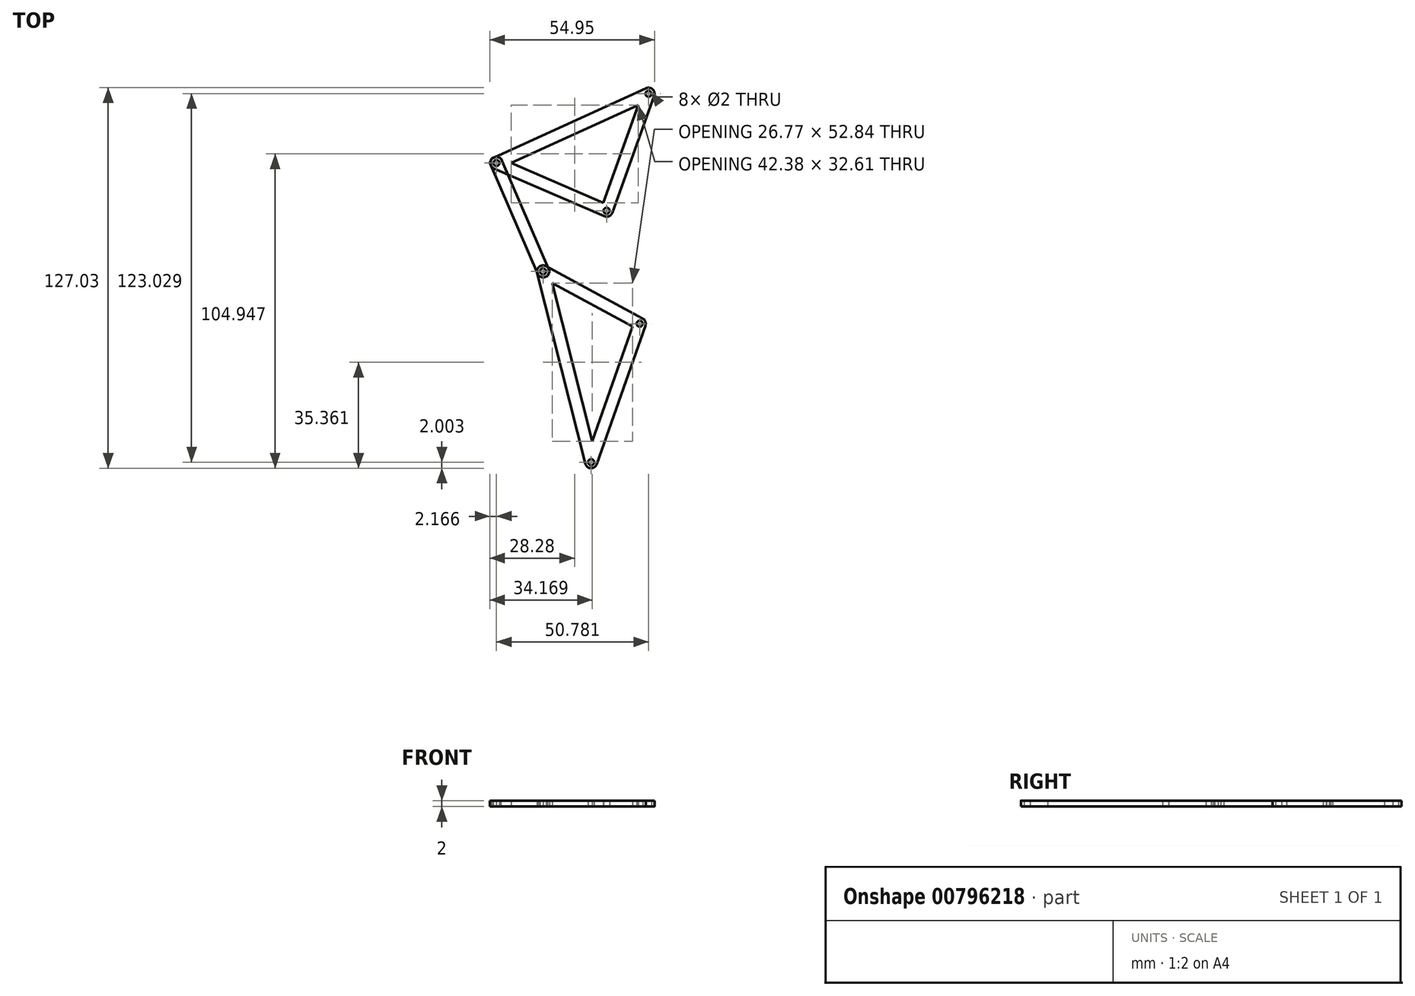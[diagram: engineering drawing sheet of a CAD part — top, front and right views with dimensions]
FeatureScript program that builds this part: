
annotation { "Feature Type Name" : "Feature", "Feature Type Description" : "" }
export const myFeature = defineFeature(function(context is Context, id is Id, definition is map)
    precondition{}
    {
        {
            var Q0;
            Q0=qCreatedBy(makeId("Top.planeOp"),FACE);
            var sketch = newSketch(context, id + "F0", { "sketchPlane" : qUnion([Q0])});
            skLineSegment(sketch, "E0", {"start": v(-38, -7.8) * mm, "end": v(-74.8, 8.14) * mm});
            skLineSegment(sketch, "E1", {"start": v(-74.8, 8.14) * mm, "end": v(-24.01, 31.27) * mm});
            skLineSegment(sketch, "E2", {"start": v(-24.01, 31.27) * mm, "end": v(-38, -7.8) * mm});
            skLineSegment(sketch, "E3", {"start": v(-24.01, 31.27) * mm, "end": v(15, 0) * mm});
            skLineSegment(sketch, "E4", {"start": v(15, 0) * mm, "end": v(0, 0) * mm});
            skLineSegment(sketch, "E5", {"start": v(-74.8, 8.14) * mm, "end": v(-59.23, -28.05) * mm});
            skLineSegment(sketch, "E6", {"start": v(-59.23, -28.05) * mm, "end": v(-26.95, -45.52) * mm});
            skLineSegment(sketch, "E7", {"start": v(-26.95, -45.52) * mm, "end": v(-38, -7.8) * mm});
            skLineSegment(sketch, "E8", {"start": v(-26.95, -45.52) * mm, "end": v(15, 0) * mm});
            skLineSegment(sketch, "E9", {"start": v(-59.23, -28.05) * mm, "end": v(-43.16, -91.76) * mm});
            skLineSegment(sketch, "E10", {"start": v(-43.16, -91.76) * mm, "end": v(-26.95, -45.52) * mm});
            skLineSegment(sketch, "E11", {"start": v(-38, -7.8) * mm, "end": v(0, -7.8) * mm, "construction": true});
            skLineSegment(sketch, "E12", {"start": v(0, -7.8) * mm, "end": v(0, 0) * mm, "construction": true});
            skSolve(sketch);
        }
        {
            assignVariable(context, id + "F1", {"name" : "thick", "anyValue" : 2});
        }
        {
            var Q0;
            Q0=qCreatedBy(makeId("Top.planeOp"),FACE);
            var sketch = newSketch(context, id + "F2", { "sketchPlane" : qUnion([Q0])});
            skCircle(sketch, "E13", {"center": v(-24.01, 31.27) * mm, "radius": 1 * mm});
            skCircle(sketch, "E14", {"center": v(-38, -7.8) * mm, "radius": 1 * mm});
            skCircle(sketch, "E15", {"center": v(-74.8, 8.14) * mm, "radius": 1 * mm});
            skArc(sketch, "E16", {"start": v(-75.62, 9.96) * mm, "mid": v(-76.8, 8.12) * mm, "end": v(-75.59, 6.3) * mm});
            skArc(sketch, "E17", {"start": v(-22.13, 30.6) * mm, "mid": v(-22.66, 32.74) * mm, "end": v(-24.84, 33.1) * mm});
            skArc(sketch, "E18", {"start": v(-38.8, -9.64) * mm, "mid": v(-37.2, -9.63) * mm, "end": v(-36.12, -8.47) * mm});
            skLineSegment(sketch, "E19", {"start": v(-75.62, 9.96) * mm, "end": v(-24.84, 33.1) * mm});
            skLineSegment(sketch, "E20", {"start": v(-22.13, 30.6) * mm, "end": v(-36.12, -8.47) * mm});
            skLineSegment(sketch, "E21", {"start": v(-38.8, -9.64) * mm, "end": v(-75.59, 6.3) * mm});
            skLineSegment(sketch, "E22.0", {"start": v(-69.87, 8.19) * mm, "end": v(-27.5, 27.5) * mm});
            skLineSegment(sketch, "E22.1", {"start": v(-39.16, -5.12) * mm, "end": v(-69.87, 8.19) * mm});
            skLineSegment(sketch, "E22.2", {"start": v(-27.5, 27.5) * mm, "end": v(-39.16, -5.12) * mm});
            skSolve(sketch);
        }
        {
            var Q0;
            Q0=makeQuery(id+"F2.imprint","IMPRINT",FACE,{"disambiguationData":[TD([[makeQuery(id+"F2.imprint","IMPRINT",EDGE,{"derivedFrom":sQuery(id+"F2.wireOp",EDGE,"E13")}),-1.0]])]});
            extrude(context, id + "F3", {"entities" : qUnion([Q0]), "depth" : (getVariable(context, 'thick')) * mm, "offsetDistance" : 25 * mm});
        }
        {
            var Q0;
            Q0=qCreatedBy(makeId("Top.planeOp"),FACE);
            var sketch = newSketch(context, id + "F4", { "sketchPlane" : qUnion([Q0])});
            skCircle(sketch, "E23", {"center": v(-26.95, -45.52) * mm, "radius": 1 * mm});
            skCircle(sketch, "E24", {"center": v(-43.16, -91.76) * mm, "radius": 1 * mm});
            skCircle(sketch, "E25", {"center": v(-59.23, -28.05) * mm, "radius": 1 * mm});
            skArc(sketch, "E26", {"start": v(-58.28, -26.3) * mm, "mid": v(-60.46, -26.47) * mm, "end": v(-61.17, -28.54) * mm});
            skArc(sketch, "E27", {"start": v(-25.06, -46.18) * mm, "mid": v(-25.09, -44.8) * mm, "end": v(-26, -43.76) * mm});
            skArc(sketch, "E28", {"start": v(-45.1, -92.25) * mm, "mid": v(-43.25, -93.75) * mm, "end": v(-41.27, -92.42) * mm});
            skLineSegment(sketch, "E29", {"start": v(-58.28, -26.3) * mm, "end": v(-26, -43.76) * mm});
            skLineSegment(sketch, "E30", {"start": v(-25.06, -46.18) * mm, "end": v(-41.27, -92.42) * mm});
            skLineSegment(sketch, "E31", {"start": v(-45.1, -92.25) * mm, "end": v(-61.17, -28.54) * mm});
            skLineSegment(sketch, "E32.0", {"start": v(-56.18, -31.98) * mm, "end": v(-29.4, -46.46) * mm});
            skLineSegment(sketch, "E32.1", {"start": v(-42.85, -84.82) * mm, "end": v(-56.18, -31.98) * mm});
            skLineSegment(sketch, "E32.2", {"start": v(-29.4, -46.46) * mm, "end": v(-42.85, -84.82) * mm});
            skSolve(sketch);
        }
        {
            var Q0;
            Q0=makeQuery(id+"F4.imprint","IMPRINT",FACE,{"disambiguationData":[TD([[makeQuery(id+"F4.imprint","IMPRINT",EDGE,{"derivedFrom":sQuery(id+"F4.wireOp",EDGE,"E23")}),-1.0]])]});
            extrude(context, id + "F5", {"entities" : qUnion([Q0]), "depth" : (getVariable(context, 'thick')) * mm, "offsetDistance" : 25 * mm});
        }
        {
            var Q0;
            Q0=qCreatedBy(makeId("Top.planeOp"),FACE);
            var sketch = newSketch(context, id + "F6", { "sketchPlane" : qUnion([Q0])});
            skCircle(sketch, "E33", {"center": v(-74.8, 8.14) * mm, "radius": 1 * mm});
            skLineSegment(sketch, "E34", {"start": v(-76.96, 8.11) * mm, "end": v(-68.85, -10.74) * mm});
            skLineSegment(sketch, "E35", {"start": v(-73.28, 9.7) * mm, "end": v(-65.18, -9.16) * mm});
            skLineSegment(sketch, "E36", {"start": v(-76.96, 8.11) * mm, "end": v(-76.35, 9.65) * mm});
            skLineSegment(sketch, "E37", {"start": v(-76.35, 9.65) * mm, "end": v(-74.82, 10.3) * mm});
            skLineSegment(sketch, "E38", {"start": v(-74.82, 10.3) * mm, "end": v(-73.28, 9.7) * mm});
            skLineSegment(sketch, "E39", {"start": v(-74.8, 8.14) * mm, "end": v(-59.23, -28.05) * mm, "construction": true});
            skLineSegment(sketch, "E40", {"start": v(-76.96, 8.11) * mm, "end": v(-73.28, 9.7) * mm, "construction": true});
            skPoint(sketch, "E41", {"position": v(-67.01, -9.95) * mm});
            skLineSegment(sketch, "E42", {"start": v(-75.8, -13.73) * mm, "end": v(-59.3, -6.64) * mm, "construction": true});
            skLineSegment(sketch, "E43.MirrorCS", {"start": v(-60.74, -29.6) * mm, "end": v(-59.2, -30.22) * mm});
            skLineSegment(sketch, "E44.MirrorCS", {"start": v(-57.68, -29.56) * mm, "end": v(-57.07, -28.02) * mm});
            skLineSegment(sketch, "E45.MirrorCS", {"start": v(-59.2, -30.22) * mm, "end": v(-57.68, -29.56) * mm});
            skLineSegment(sketch, "E46.MirrorCS", {"start": v(-60.74, -29.6) * mm, "end": v(-57.07, -28.02) * mm, "construction": true});
            skLineSegment(sketch, "E47.MirrorCS", {"start": v(-57.07, -28.02) * mm, "end": v(-65.18, -9.16) * mm});
            skLineSegment(sketch, "E48.MirrorCS", {"start": v(-60.74, -29.6) * mm, "end": v(-68.85, -10.74) * mm});
            skCircle(sketch, "E49.MirrorC", {"center": v(-59.23, -28.05) * mm, "radius": 1 * mm});
            skSolve(sketch);
        }
        {
            var Q0;
            Q0=makeQuery(id+"F6.imprint","IMPRINT",FACE,{"disambiguationData":[TD([[makeQuery(id+"F6.imprint","IMPRINT",EDGE,{"derivedFrom":sQuery(id+"F6.wireOp",EDGE,"E33")}),-1.0]])]});
            extrude(context, id + "F7", {"entities" : qUnion([Q0]), "depth" : (getVariable(context, 'thick')) * mm, "offsetDistance" : 25 * mm});
        }
    });
